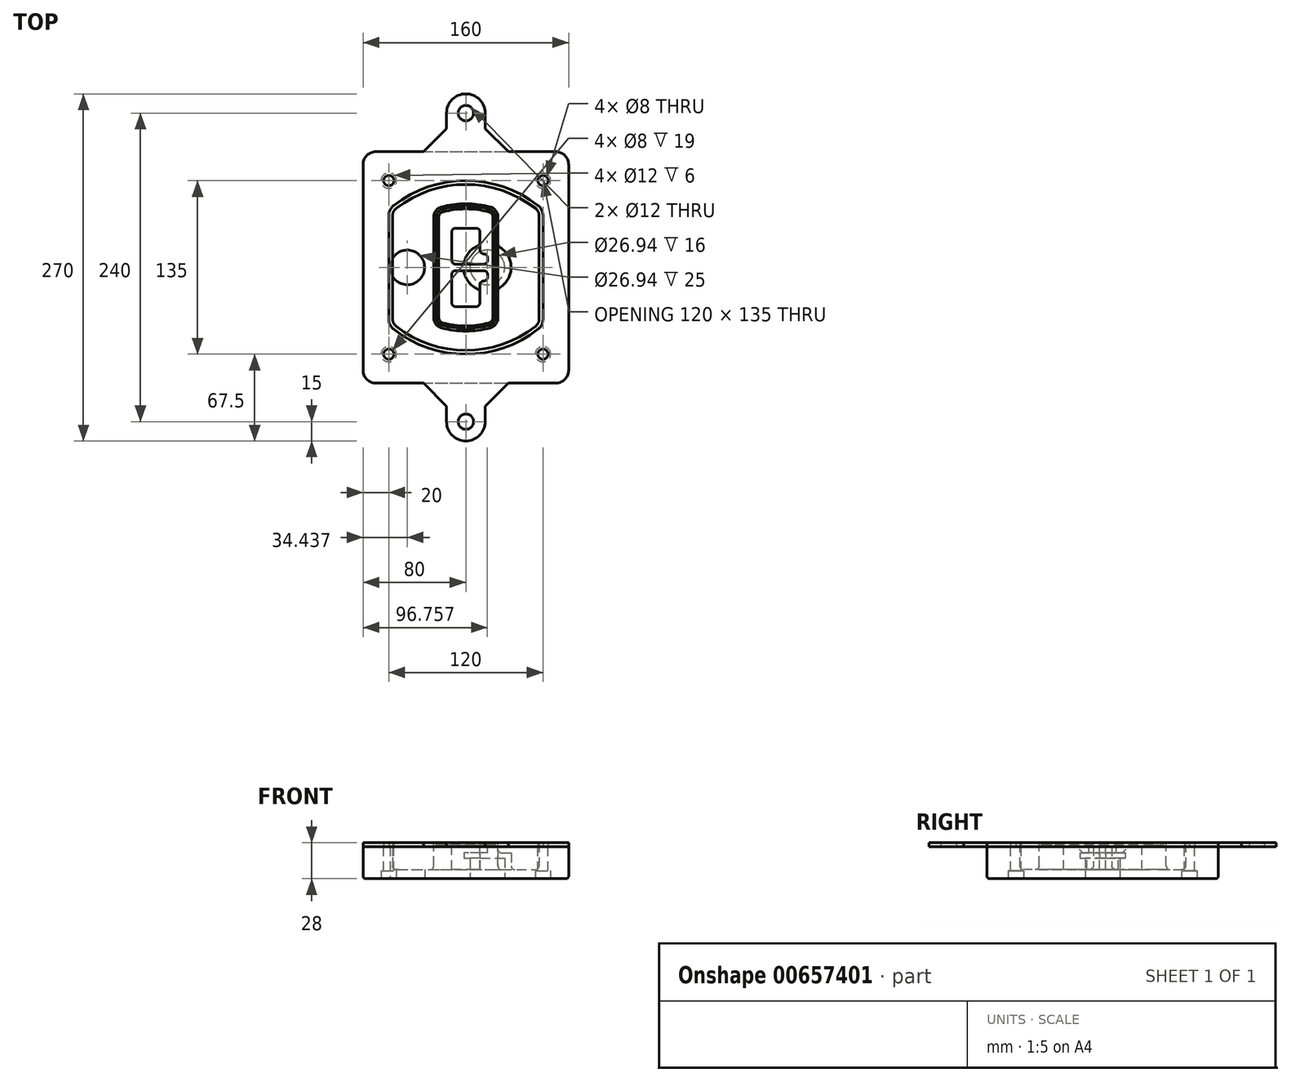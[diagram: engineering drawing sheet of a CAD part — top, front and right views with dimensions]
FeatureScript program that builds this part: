
annotation { "Feature Type Name" : "Feature", "Feature Type Description" : "" }
export const myFeature = defineFeature(function(context is Context, id is Id, definition is map)
    precondition{}
    {
        {
            var Q0;
            Q0=qCreatedBy(makeId("Top.planeOp"),FACE);
            var sketch = newSketch(context, id + "F0", { "sketchPlane" : qUnion([Q0])});
            skPoint(sketch, "E0.rect.middle", {"position": v(0, 0) * mm});
            skLineSegment(sketch, "E1.bottom", {"start": v(-70, -90) * mm, "end": v(70, -90) * mm});
            skLineSegment(sketch, "E1.top", {"start": v(-70, 90) * mm, "end": v(70, 90) * mm});
            skLineSegment(sketch, "E1.left", {"start": v(-80, -80) * mm, "end": v(-80, 80) * mm});
            skLineSegment(sketch, "E1.right", {"start": v(80, -80) * mm, "end": v(80, 80) * mm});
            skLineSegment(sketch, "E2", {"start": v(-80, 90) * mm, "end": v(80, -90) * mm, "construction": true});
            skLineSegment(sketch, "E3", {"start": v(80, 90) * mm, "end": v(-80, -90) * mm, "construction": true});
            skCircle(sketch, "E4", {"center": v(-60, 67.5) * mm, "radius": 4 * mm});
            skCircle(sketch, "E5", {"center": v(60, 67.5) * mm, "radius": 4 * mm});
            skCircle(sketch, "E6", {"center": v(60, -67.5) * mm, "radius": 4 * mm});
            skCircle(sketch, "E7", {"center": v(-60, -67.5) * mm, "radius": 4 * mm});
            skLineSegment(sketch, "E8", {"start": v(-60, 67.5) * mm, "end": v(60, 67.5) * mm, "construction": true});
            skLineSegment(sketch, "E9", {"start": v(60, 67.5) * mm, "end": v(60, -67.5) * mm, "construction": true});
            skLineSegment(sketch, "E10", {"start": v(60, -67.5) * mm, "end": v(-60, -67.5) * mm, "construction": true});
            skLineSegment(sketch, "E11", {"start": v(-60, -67.5) * mm, "end": v(-60, 67.5) * mm, "construction": true});
            skLineSegment(sketch, "E12", {"start": v(-60, 40.3) * mm, "end": v(-60, -40.3) * mm});
            skLineSegment(sketch, "E13", {"start": v(60, 40.3) * mm, "end": v(60, -40.3) * mm});
            skArc(sketch, "E14", {"start": v(56.15, 48.18) * mm, "mid": v(0, 67.5) * mm, "end": v(-56.15, 48.18) * mm});
            skArc(sketch, "E15", {"start": v(-56.15, -48.18) * mm, "mid": v(0, -67.5) * mm, "end": v(56.15, -48.18) * mm});
            skLineSegment(sketch, "E16", {"start": v(-60, 0) * mm, "end": v(60, 0) * mm, "construction": true});
            skPoint(sketch, "E17.visualSharp", {"position": v(-60, -45) * mm});
            skArc(sketch, "E17.filletArc", {"start": v(-60, -40.3) * mm, "mid": v(-58.99, -44.68) * mm, "end": v(-56.15, -48.18) * mm});
            skPoint(sketch, "E18.visualSharp", {"position": v(-60, 45) * mm});
            skArc(sketch, "E18.filletArc", {"start": v(-56.15, 48.18) * mm, "mid": v(-58.99, 44.68) * mm, "end": v(-60, 40.3) * mm});
            skPoint(sketch, "E19.visualSharp", {"position": v(60, 45) * mm});
            skArc(sketch, "E19.filletArc", {"start": v(60, 40.3) * mm, "mid": v(58.99, 44.68) * mm, "end": v(56.15, 48.18) * mm});
            skPoint(sketch, "E20.visualSharp", {"position": v(60, -45) * mm});
            skArc(sketch, "E20.filletArc", {"start": v(56.15, -48.18) * mm, "mid": v(58.99, -44.68) * mm, "end": v(60, -40.3) * mm});
            skPoint(sketch, "E21.visualSharp", {"position": v(-80, 90) * mm});
            skArc(sketch, "E21.filletArc", {"start": v(-70, 90) * mm, "mid": v(-77.07, 87.07) * mm, "end": v(-80, 80) * mm});
            skPoint(sketch, "E22.visualSharp", {"position": v(80, 90) * mm});
            skArc(sketch, "E22.filletArc", {"start": v(80, 80) * mm, "mid": v(77.07, 87.07) * mm, "end": v(70, 90) * mm});
            skPoint(sketch, "E23.visualSharp", {"position": v(80, -90) * mm});
            skArc(sketch, "E23.filletArc", {"start": v(70, -90) * mm, "mid": v(77.07, -87.07) * mm, "end": v(80, -80) * mm});
            skPoint(sketch, "E24.visualSharp", {"position": v(-80, -90) * mm});
            skArc(sketch, "E24.filletArc", {"start": v(-80, -80) * mm, "mid": v(-77.07, -87.07) * mm, "end": v(-70, -90) * mm});
            skArc(sketch, "E25.0", {"start": v(57, 40.3) * mm, "mid": v(56.3, 43.36) * mm, "end": v(54.3, 45.81) * mm});
            skLineSegment(sketch, "E25.1", {"start": v(57, 40.3) * mm, "end": v(57, -40.3) * mm});
            skArc(sketch, "E25.2", {"start": v(54.3, -45.81) * mm, "mid": v(56.3, -43.36) * mm, "end": v(57, -40.3) * mm});
            skArc(sketch, "E25.3", {"start": v(-54.3, -45.81) * mm, "mid": v(0, -64.5) * mm, "end": v(54.3, -45.81) * mm});
            skArc(sketch, "E25.4", {"start": v(-57, -40.3) * mm, "mid": v(-56.3, -43.36) * mm, "end": v(-54.3, -45.81) * mm});
            skArc(sketch, "E25.5", {"start": v(54.3, 45.81) * mm, "mid": v(0, 64.5) * mm, "end": v(-54.3, 45.81) * mm});
            skLineSegment(sketch, "E25.6", {"start": v(-57, 40.3) * mm, "end": v(-57, -40.3) * mm});
            skArc(sketch, "E25.7", {"start": v(-54.3, 45.81) * mm, "mid": v(-56.3, 43.36) * mm, "end": v(-57, 40.3) * mm});
            skArc(sketch, "E26.0", {"start": v(-58.62, 51.33) * mm, "mid": v(-62.58, 46.43) * mm, "end": v(-64, 40.3) * mm});
            skArc(sketch, "E26.1", {"start": v(58.62, 51.33) * mm, "mid": v(0, 71.5) * mm, "end": v(-58.62, 51.33) * mm});
            skArc(sketch, "E26.2", {"start": v(64, 40.3) * mm, "mid": v(62.58, 46.43) * mm, "end": v(58.62, 51.33) * mm});
            skLineSegment(sketch, "E26.3", {"start": v(64, 40.3) * mm, "end": v(64, -40.3) * mm});
            skArc(sketch, "E26.4", {"start": v(58.62, -51.33) * mm, "mid": v(62.58, -46.43) * mm, "end": v(64, -40.3) * mm});
            skLineSegment(sketch, "E26.5", {"start": v(-64, 40.3) * mm, "end": v(-64, -40.3) * mm});
            skArc(sketch, "E26.6", {"start": v(-58.62, -51.33) * mm, "mid": v(0, -71.5) * mm, "end": v(58.62, -51.33) * mm});
            skArc(sketch, "E26.7", {"start": v(-64, -40.3) * mm, "mid": v(-62.58, -46.43) * mm, "end": v(-58.62, -51.33) * mm});
            skSolve(sketch);
        }
        {
            var Q0;
            Q0=makeQuery(id+"F0.imprint","IMPRINT",FACE,{"disambiguationData":[TD([[makeQuery(id+"F0.imprint","IMPRINT",EDGE,{"derivedFrom":sQuery(id+"F0.wireOp",EDGE,"E1.bottom")}),1.0]])]});
            var Q1;
            Q1=makeQuery(id+"F0.imprint","IMPRINT",FACE,{"disambiguationData":[TD([[makeQuery(id+"F0.imprint","IMPRINT",EDGE,{"derivedFrom":sQuery(id+"F0.wireOp",EDGE,"E12")}),1.0]])]});
            var Q2;
            Q2=makeQuery(id+"F0.imprint","IMPRINT",FACE,{"disambiguationData":[TD([[makeQuery(id+"F0.imprint","IMPRINT",EDGE,{"derivedFrom":sQuery(id+"F0.wireOp",EDGE,"E25.0")}),1.0]])]});
            var Q3;
            Q3=makeQuery(id+"F0.imprint","IMPRINT",FACE,{"disambiguationData":[TD([[makeQuery(id+"F0.imprint","IMPRINT",EDGE,{"derivedFrom":sQuery(id+"F0.wireOp",EDGE,"E12")}),-1.0]])]});
            extrude(context, id + "F1", {"entities" : qUnion([Q0, Q1, Q2, Q3]), "oppositeDirection" : true, "depth" : 25 * mm});
        }
        {
            var Q0;
            Q0=makeQuery(id+"F0.imprint","IMPRINT",FACE,{"disambiguationData":[TD([[makeQuery(id+"F0.imprint","IMPRINT",EDGE,{"derivedFrom":sQuery(id+"F0.wireOp",EDGE,"E12")}),1.0]])]});
            extrude(context, id + "F2", {"entities" : qUnion([Q0]), "operationType" : NewBodyOperationType.ADD, "depth" : 3 * mm});
        }
        {
            var Q0;
            Q0=makeQuery(id+"F0.imprint","IMPRINT",FACE,{"disambiguationData":[TD([[makeQuery(id+"F0.imprint","IMPRINT",EDGE,{"derivedFrom":sQuery(id+"F0.wireOp",EDGE,"E25.0")}),1.0]])]});
            extrude(context, id + "F3", {"entities" : qUnion([Q0]), "operationType" : NewBodyOperationType.REMOVE, "oppositeDirection" : true, "depth" : 18 * mm});
        }
        {
            var Q0;
            Q0=makeQuery(id+"F2.opExtrude","CAP_FACE",FACE,{"disambiguationData":[OSD([sQuery(id+"F0.wireOp",EDGE,"E12"),sQuery(id+"F0.wireOp",EDGE,"E13"),sQuery(id+"F0.wireOp",EDGE,"E14"),sQuery(id+"F0.wireOp",EDGE,"E15"),sQuery(id+"F0.wireOp",EDGE,"E17.filletArc"),sQuery(id+"F0.wireOp",EDGE,"E18.filletArc"),sQuery(id+"F0.wireOp",EDGE,"E19.filletArc"),sQuery(id+"F0.wireOp",EDGE,"E20.filletArc"),sQuery(id+"F0.wireOp",EDGE,"E25.0"),sQuery(id+"F0.wireOp",EDGE,"E25.1"),sQuery(id+"F0.wireOp",EDGE,"E25.2"),sQuery(id+"F0.wireOp",EDGE,"E25.3"),sQuery(id+"F0.wireOp",EDGE,"E25.4"),sQuery(id+"F0.wireOp",EDGE,"E25.5"),sQuery(id+"F0.wireOp",EDGE,"E25.6"),sQuery(id+"F0.wireOp",EDGE,"E25.7")])],"isStart":false});
            var sketch = newSketch(context, id + "F4", { "sketchPlane" : qUnion([Q0])});
            skArc(sketch, "E27.0", {"start": v(-19.08, -46.97) * mm, "mid": v(0, -49.5) * mm, "end": v(19.08, -46.97) * mm});
            skArc(sketch, "E28.0", {"start": v(19.08, 46.97) * mm, "mid": v(0, 49.5) * mm, "end": v(-19.08, 46.97) * mm});
            skLineSegment(sketch, "E29", {"start": v(-25, 39.25) * mm, "end": v(-25, -39.25) * mm});
            skLineSegment(sketch, "E30", {"start": v(25, 39.25) * mm, "end": v(25, -39.25) * mm});
            skLineSegment(sketch, "E31", {"start": v(-25, 45.1) * mm, "end": v(25, 45.1) * mm, "construction": true});
            skLineSegment(sketch, "E32", {"start": v(-25, -45.1) * mm, "end": v(25, -45.1) * mm, "construction": true});
            skPoint(sketch, "E33.visualSharp", {"position": v(-25, 45.1) * mm});
            skArc(sketch, "E33.filletArc", {"start": v(-19.08, 46.97) * mm, "mid": v(-23.35, 44.11) * mm, "end": v(-25, 39.25) * mm});
            skPoint(sketch, "E34.visualSharp", {"position": v(25, 45.1) * mm});
            skArc(sketch, "E34.filletArc", {"start": v(25, 39.25) * mm, "mid": v(23.35, 44.11) * mm, "end": v(19.08, 46.97) * mm});
            skPoint(sketch, "E35.visualSharp", {"position": v(25, -45.1) * mm});
            skArc(sketch, "E35.filletArc", {"start": v(19.08, -46.97) * mm, "mid": v(23.35, -44.11) * mm, "end": v(25, -39.25) * mm});
            skPoint(sketch, "E36.visualSharp", {"position": v(-25, -45.1) * mm});
            skArc(sketch, "E36.filletArc", {"start": v(-25, -39.25) * mm, "mid": v(-23.35, -44.11) * mm, "end": v(-19.08, -46.97) * mm});
            skArc(sketch, "E37.0", {"start": v(54.3, 45.81) * mm, "mid": v(0, 64.5) * mm, "end": v(-54.3, 45.81) * mm});
            skArc(sketch, "E37.1", {"start": v(-54.3, 45.81) * mm, "mid": v(-56.3, 43.36) * mm, "end": v(-57, 40.3) * mm});
            skLineSegment(sketch, "E37.2", {"start": v(-57, 40.3) * mm, "end": v(-57, -40.3) * mm});
            skArc(sketch, "E37.3", {"start": v(-57, -40.3) * mm, "mid": v(-56.3, -43.36) * mm, "end": v(-54.3, -45.81) * mm});
            skArc(sketch, "E37.4", {"start": v(-54.3, -45.81) * mm, "mid": v(0, -64.5) * mm, "end": v(54.3, -45.81) * mm});
            skArc(sketch, "E37.5", {"start": v(54.3, -45.81) * mm, "mid": v(56.3, -43.36) * mm, "end": v(57, -40.3) * mm});
            skLineSegment(sketch, "E37.6", {"start": v(57, 40.3) * mm, "end": v(57, -40.3) * mm});
            skArc(sketch, "E37.7", {"start": v(57, 40.3) * mm, "mid": v(56.3, 43.36) * mm, "end": v(54.3, 45.81) * mm});
            skLineSegment(sketch, "E38.0", {"start": v(23, 39.25) * mm, "end": v(23, -39.25) * mm});
            skArc(sketch, "E38.1", {"start": v(18.56, -45.04) * mm, "mid": v(21.76, -42.9) * mm, "end": v(23, -39.25) * mm});
            skArc(sketch, "E38.2", {"start": v(-18.56, -45.04) * mm, "mid": v(0, -47.5) * mm, "end": v(18.56, -45.04) * mm});
            skArc(sketch, "E38.3", {"start": v(-23, -39.25) * mm, "mid": v(-21.76, -42.9) * mm, "end": v(-18.56, -45.04) * mm});
            skLineSegment(sketch, "E38.4", {"start": v(-23, 39.25) * mm, "end": v(-23, -39.25) * mm});
            skArc(sketch, "E38.5", {"start": v(23, 39.25) * mm, "mid": v(21.76, 42.9) * mm, "end": v(18.56, 45.04) * mm});
            skArc(sketch, "E38.6", {"start": v(-18.56, 45.04) * mm, "mid": v(-21.76, 42.9) * mm, "end": v(-23, 39.25) * mm});
            skArc(sketch, "E38.7", {"start": v(18.56, 45.04) * mm, "mid": v(0, 47.5) * mm, "end": v(-18.56, 45.04) * mm});
            skArc(sketch, "E39.0", {"start": v(21, 39.25) * mm, "mid": v(20.18, 41.68) * mm, "end": v(18.04, 43.1) * mm});
            skLineSegment(sketch, "E39.1", {"start": v(21, 39.25) * mm, "end": v(21, -39.25) * mm});
            skArc(sketch, "E39.2", {"start": v(18.04, -43.1) * mm, "mid": v(20.18, -41.68) * mm, "end": v(21, -39.25) * mm});
            skArc(sketch, "E39.3", {"start": v(-18.04, -43.1) * mm, "mid": v(0, -45.5) * mm, "end": v(18.04, -43.1) * mm});
            skArc(sketch, "E39.4", {"start": v(-21, -39.25) * mm, "mid": v(-20.18, -41.68) * mm, "end": v(-18.04, -43.1) * mm});
            skArc(sketch, "E39.5", {"start": v(18.04, 43.1) * mm, "mid": v(0, 45.5) * mm, "end": v(-18.04, 43.1) * mm});
            skLineSegment(sketch, "E39.6", {"start": v(-21, 39.25) * mm, "end": v(-21, -39.25) * mm});
            skArc(sketch, "E39.7", {"start": v(-18.04, 43.1) * mm, "mid": v(-20.18, 41.68) * mm, "end": v(-21, 39.25) * mm});
            skLineSegment(sketch, "E40", {"start": v(-25, 0) * mm, "end": v(25, 0) * mm, "construction": true});
            skLineSegment(sketch, "E41", {"start": v(-11, 5.5) * mm, "end": v(-11, 27.5) * mm});
            skLineSegment(sketch, "E42", {"start": v(-8, 30.5) * mm, "end": v(8, 30.5) * mm});
            skLineSegment(sketch, "E43", {"start": v(11, 27.5) * mm, "end": v(11, 13.5) * mm});
            skLineSegment(sketch, "E44", {"start": v(14, 10.5) * mm, "end": v(14, 10.5) * mm});
            skLineSegment(sketch, "E45", {"start": v(17, 7.5) * mm, "end": v(17, 5.5) * mm});
            skLineSegment(sketch, "E46", {"start": v(14, 2.5) * mm, "end": v(-8, 2.5) * mm});
            skPoint(sketch, "E47.visualSharp", {"position": v(-11, 30.5) * mm});
            skArc(sketch, "E47.filletArc", {"start": v(-8, 30.5) * mm, "mid": v(-10.12, 29.62) * mm, "end": v(-11, 27.5) * mm});
            skPoint(sketch, "E48.visualSharp", {"position": v(11, 30.5) * mm});
            skArc(sketch, "E48.filletArc", {"start": v(11, 27.5) * mm, "mid": v(10.12, 29.62) * mm, "end": v(8, 30.5) * mm});
            skPoint(sketch, "E49.visualSharp", {"position": v(11, 10.5) * mm});
            skArc(sketch, "E49.filletArc", {"start": v(11, 13.5) * mm, "mid": v(11.88, 11.38) * mm, "end": v(14, 10.5) * mm});
            skPoint(sketch, "E50.visualSharp", {"position": v(17, 10.5) * mm});
            skArc(sketch, "E50.filletArc", {"start": v(17, 7.5) * mm, "mid": v(16.12, 9.62) * mm, "end": v(14, 10.5) * mm});
            skPoint(sketch, "E51.visualSharp", {"position": v(17, 2.5) * mm});
            skArc(sketch, "E51.filletArc", {"start": v(14, 2.5) * mm, "mid": v(16.12, 3.38) * mm, "end": v(17, 5.5) * mm});
            skPoint(sketch, "E52.visualSharp", {"position": v(-11, 2.5) * mm});
            skArc(sketch, "E52.filletArc", {"start": v(-11, 5.5) * mm, "mid": v(-10.12, 3.38) * mm, "end": v(-8, 2.5) * mm});
            skLineSegment(sketch, "E53.0.MirrorCS", {"start": v(14, -2.5) * mm, "end": v(-8, -2.5) * mm});
            skArc(sketch, "E54.0.MirrorCS", {"start": v(-11, -5.5) * mm, "mid": v(-10.12, -3.38) * mm, "end": v(-8, -2.5) * mm});
            skLineSegment(sketch, "E55.0.MirrorCS", {"start": v(-11, -5.5) * mm, "end": v(-11, -27.5) * mm});
            skArc(sketch, "E56.0.MirrorCS", {"start": v(-8, -30.5) * mm, "mid": v(-10.12, -29.62) * mm, "end": v(-11, -27.5) * mm});
            skLineSegment(sketch, "E57.0.MirrorCS", {"start": v(-8, -30.5) * mm, "end": v(8, -30.5) * mm});
            skArc(sketch, "E58.0.MirrorCS", {"start": v(11, -27.5) * mm, "mid": v(10.12, -29.62) * mm, "end": v(8, -30.5) * mm});
            skLineSegment(sketch, "E59.0.MirrorCS", {"start": v(11, -27.5) * mm, "end": v(11, -13.5) * mm});
            skArc(sketch, "E60.0.MirrorCS", {"start": v(11, -13.5) * mm, "mid": v(11.88, -11.38) * mm, "end": v(14, -10.5) * mm});
            skArc(sketch, "E61.0.MirrorCS", {"start": v(17, -7.5) * mm, "mid": v(16.12, -9.62) * mm, "end": v(14, -10.5) * mm});
            skLineSegment(sketch, "E62.0.MirrorCS", {"start": v(17, -7.5) * mm, "end": v(17, -5.5) * mm});
            skArc(sketch, "E63.0.MirrorCS", {"start": v(14, -2.5) * mm, "mid": v(16.12, -3.38) * mm, "end": v(17, -5.5) * mm});
            skSolve(sketch);
        }
        {
            var Q0;
            Q0=makeQuery(id+"F4.imprint","IMPRINT",FACE,{"disambiguationData":[TD([[makeQuery(id+"F4.imprint","IMPRINT",EDGE,{"derivedFrom":sQuery(id+"F4.wireOp",EDGE,"E27.0")}),1.0]])]});
            var Q1;
            Q1=makeQuery(id+"F4.imprint","IMPRINT",FACE,{"disambiguationData":[TD([[makeQuery(id+"F4.imprint","IMPRINT",EDGE,{"derivedFrom":sQuery(id+"F4.wireOp",EDGE,"E38.0")}),-1.0]])]});
            var Q2;
            Q2=makeQuery(id+"F4.imprint","IMPRINT",FACE,{"disambiguationData":[TD([[makeQuery(id+"F4.imprint","IMPRINT",EDGE,{"derivedFrom":sQuery(id+"F4.wireOp",EDGE,"E39.0")}),1.0]])]});
            extrude(context, id + "F5", {"entities" : qUnion([Q0, Q1, Q2]), "operationType" : NewBodyOperationType.ADD, "endBound" : BoundingType.UP_TO_NEXT, "oppositeDirection" : true, "depth" : 25 * mm});
        }
        {
            var Q0;
            Q0=makeQuery(id+"F4.imprint","IMPRINT",FACE,{"disambiguationData":[TD([[makeQuery(id+"F4.imprint","IMPRINT",EDGE,{"derivedFrom":sQuery(id+"F4.wireOp",EDGE,"E38.0")}),-1.0]])]});
            extrude(context, id + "F6", {"entities" : qUnion([Q0]), "operationType" : NewBodyOperationType.REMOVE, "oppositeDirection" : true, "depth" : 2 * mm});
        }
        {
            var Q0;
            Q0=makeQuery(id+"F1.opExtrude","CAP_FACE",FACE,{"disambiguationData":[OSD([sQuery(id+"F0.wireOp",EDGE,"E1.bottom"),sQuery(id+"F0.wireOp",EDGE,"E1.top"),sQuery(id+"F0.wireOp",EDGE,"E1.left"),sQuery(id+"F0.wireOp",EDGE,"E1.right"),sQuery(id+"F0.wireOp",EDGE,"E4"),sQuery(id+"F0.wireOp",EDGE,"E5"),sQuery(id+"F0.wireOp",EDGE,"E6"),sQuery(id+"F0.wireOp",EDGE,"E7"),sQuery(id+"F0.wireOp",EDGE,"E21.filletArc"),sQuery(id+"F0.wireOp",EDGE,"E22.filletArc"),sQuery(id+"F0.wireOp",EDGE,"E23.filletArc"),sQuery(id+"F0.wireOp",EDGE,"E24.filletArc")])],"isStart":false});
            var sketch = newSketch(context, id + "F7", { "sketchPlane" : qUnion([Q0])});
            skCircle(sketch, "E64", {"center": v(16.76, 0) * mm, "radius": 13.47 * mm});
            skCircle(sketch, "E65", {"center": v(-45.56, 0) * mm, "radius": 13.47 * mm});
            skLineSegment(sketch, "E66", {"start": v(80, 0) * mm, "end": v(-80, 0) * mm});
            skCircle(sketch, "E67", {"center": v(16.76, 0) * mm, "radius": 18.47 * mm});
            skCircle(sketch, "E68", {"center": v(60, -67.5) * mm, "radius": 6 * mm});
            skCircle(sketch, "E69", {"center": v(-60, -67.5) * mm, "radius": 6 * mm});
            skCircle(sketch, "E70", {"center": v(-60, 67.5) * mm, "radius": 6 * mm});
            skCircle(sketch, "E71", {"center": v(60, 67.5) * mm, "radius": 6 * mm});
            skSolve(sketch);
        }
        {
            var Q0;
            {var subQ1=sQuery(id+"F7.wireOp",EDGE,"E66");var subQ4=sQuery(id+"F7.wireOp",EDGE,"E64");var subQ6=makeQuery(id+"F7.imprint","INTERSECT",VERTEX,{"disambiguationData":[OD(0.0)],"derivedFrom":[subQ4,subQ1]});Q0=makeQuery(id+"F7.imprint","IMPRINT",FACE,{"disambiguationData":[TD([[makeQuery(id+"F7.imprint","IMPRINT",EDGE,{"disambiguationData":[TD([[subQ6,-1.0]])],"derivedFrom":subQ4}),-1.0]])]});}
            var Q1;
            {var subQ0=sQuery(id+"F7.wireOp",EDGE,"E66");var subQ1=sQuery(id+"F7.wireOp",EDGE,"E64");var subQ3=makeQuery(id+"F7.imprint","INTERSECT",VERTEX,{"disambiguationData":[OD(0.0)],"derivedFrom":[subQ1,subQ0]});Q1=makeQuery(id+"F7.imprint","IMPRINT",FACE,{"disambiguationData":[TD([[makeQuery(id+"F7.imprint","IMPRINT",EDGE,{"disambiguationData":[TD([[subQ3,-1.0]])],"derivedFrom":subQ1}),1.0]])]});}
            var Q2;
            {var subQ0=sQuery(id+"F7.wireOp",EDGE,"E66");var subQ1=sQuery(id+"F7.wireOp",EDGE,"E64");var subQ3=makeQuery(id+"F7.imprint","INTERSECT",VERTEX,{"disambiguationData":[OD(0.0)],"derivedFrom":[subQ1,subQ0]});Q2=makeQuery(id+"F7.imprint","IMPRINT",FACE,{"disambiguationData":[TD([[makeQuery(id+"F7.imprint","IMPRINT",EDGE,{"disambiguationData":[TD([[subQ3,1.0]])],"derivedFrom":subQ1}),1.0]])]});}
            var Q3;
            {var subQ1=sQuery(id+"F7.wireOp",EDGE,"E66");var subQ4=sQuery(id+"F7.wireOp",EDGE,"E64");var subQ6=makeQuery(id+"F7.imprint","INTERSECT",VERTEX,{"disambiguationData":[OD(0.0)],"derivedFrom":[subQ4,subQ1]});Q3=makeQuery(id+"F7.imprint","IMPRINT",FACE,{"disambiguationData":[TD([[makeQuery(id+"F7.imprint","IMPRINT",EDGE,{"disambiguationData":[TD([[subQ6,1.0]])],"derivedFrom":subQ4}),-1.0]])]});}
            extrude(context, id + "F8", {"entities" : qUnion([Q0, Q1, Q2, Q3]), "operationType" : NewBodyOperationType.ADD, "oppositeDirection" : true, "depth" : 20 * mm});
        }
        {
            var Q0;
            {var subQ0=sQuery(id+"F7.wireOp",EDGE,"E66");var subQ1=sQuery(id+"F7.wireOp",EDGE,"E64");var subQ3=makeQuery(id+"F7.imprint","INTERSECT",VERTEX,{"disambiguationData":[OD(0.0)],"derivedFrom":[subQ1,subQ0]});Q0=makeQuery(id+"F7.imprint","IMPRINT",FACE,{"disambiguationData":[TD([[makeQuery(id+"F7.imprint","IMPRINT",EDGE,{"disambiguationData":[TD([[subQ3,-1.0]])],"derivedFrom":subQ1}),1.0]])]});}
            var Q1;
            {var subQ0=sQuery(id+"F7.wireOp",EDGE,"E66");var subQ1=sQuery(id+"F7.wireOp",EDGE,"E64");var subQ3=makeQuery(id+"F7.imprint","INTERSECT",VERTEX,{"disambiguationData":[OD(0.0)],"derivedFrom":[subQ1,subQ0]});Q1=makeQuery(id+"F7.imprint","IMPRINT",FACE,{"disambiguationData":[TD([[makeQuery(id+"F7.imprint","IMPRINT",EDGE,{"disambiguationData":[TD([[subQ3,1.0]])],"derivedFrom":subQ1}),1.0]])]});}
            extrude(context, id + "F9", {"entities" : qUnion([Q0, Q1]), "operationType" : NewBodyOperationType.REMOVE, "oppositeDirection" : true, "depth" : 16 * mm});
        }
        {
            var Q0;
            {var subQ0=sQuery(id+"F7.wireOp",EDGE,"E66");var subQ1=sQuery(id+"F7.wireOp",EDGE,"E65");var subQ3=makeQuery(id+"F7.imprint","INTERSECT",VERTEX,{"disambiguationData":[OD(0.0)],"derivedFrom":[subQ1,subQ0]});Q0=makeQuery(id+"F7.imprint","IMPRINT",FACE,{"disambiguationData":[TD([[makeQuery(id+"F7.imprint","IMPRINT",EDGE,{"disambiguationData":[TD([[subQ3,-1.0]])],"derivedFrom":subQ1}),1.0]])]});}
            var Q1;
            {var subQ0=sQuery(id+"F7.wireOp",EDGE,"E66");var subQ1=sQuery(id+"F7.wireOp",EDGE,"E65");var subQ3=makeQuery(id+"F7.imprint","INTERSECT",VERTEX,{"disambiguationData":[OD(0.0)],"derivedFrom":[subQ1,subQ0]});Q1=makeQuery(id+"F7.imprint","IMPRINT",FACE,{"disambiguationData":[TD([[makeQuery(id+"F7.imprint","IMPRINT",EDGE,{"disambiguationData":[TD([[subQ3,1.0]])],"derivedFrom":subQ1}),1.0]])]});}
            extrude(context, id + "F10", {"entities" : qUnion([Q0, Q1]), "operationType" : NewBodyOperationType.REMOVE, "oppositeDirection" : true, "depth" : 25 * mm});
        }
        {
            var Q0;
            Q0=makeQuery(id+"F7.imprint","IMPRINT",FACE,{"disambiguationData":[TD([[makeQuery(id+"F7.imprint","IMPRINT",EDGE,{"derivedFrom":sQuery(id+"F7.wireOp",EDGE,"E68")}),1.0]])]});
            var Q1;
            Q1=makeQuery(id+"F7.imprint","IMPRINT",FACE,{"disambiguationData":[TD([[makeQuery(id+"F7.imprint","IMPRINT",EDGE,{"derivedFrom":makeQuery(id+"F1.opExtrude","CAP_EDGE",EDGE,{"disambiguationData":[OSD([sQuery(id+"F0.wireOp",EDGE,"E5")])],"isStart":false})}),-1.0]])]});
            var Q2;
            Q2=makeQuery(id+"F7.imprint","IMPRINT",FACE,{"disambiguationData":[TD([[makeQuery(id+"F7.imprint","IMPRINT",EDGE,{"derivedFrom":sQuery(id+"F7.wireOp",EDGE,"E69")}),1.0]])]});
            var Q3;
            Q3=makeQuery(id+"F7.imprint","IMPRINT",FACE,{"disambiguationData":[TD([[makeQuery(id+"F7.imprint","IMPRINT",EDGE,{"derivedFrom":makeQuery(id+"F1.opExtrude","CAP_EDGE",EDGE,{"disambiguationData":[OSD([sQuery(id+"F0.wireOp",EDGE,"E4")])],"isStart":false})}),-1.0]])]});
            var Q4;
            Q4=makeQuery(id+"F7.imprint","IMPRINT",FACE,{"disambiguationData":[TD([[makeQuery(id+"F7.imprint","IMPRINT",EDGE,{"derivedFrom":sQuery(id+"F7.wireOp",EDGE,"E70")}),1.0]])]});
            var Q5;
            Q5=makeQuery(id+"F7.imprint","IMPRINT",FACE,{"disambiguationData":[TD([[makeQuery(id+"F7.imprint","IMPRINT",EDGE,{"derivedFrom":makeQuery(id+"F1.opExtrude","CAP_EDGE",EDGE,{"disambiguationData":[OSD([sQuery(id+"F0.wireOp",EDGE,"E7")])],"isStart":false})}),-1.0]])]});
            var Q6;
            Q6=makeQuery(id+"F7.imprint","IMPRINT",FACE,{"disambiguationData":[TD([[makeQuery(id+"F7.imprint","IMPRINT",EDGE,{"derivedFrom":sQuery(id+"F7.wireOp",EDGE,"E71")}),1.0]])]});
            var Q7;
            Q7=makeQuery(id+"F7.imprint","IMPRINT",FACE,{"disambiguationData":[TD([[makeQuery(id+"F7.imprint","IMPRINT",EDGE,{"derivedFrom":makeQuery(id+"F1.opExtrude","CAP_EDGE",EDGE,{"disambiguationData":[OSD([sQuery(id+"F0.wireOp",EDGE,"E6")])],"isStart":false})}),-1.0]])]});
            extrude(context, id + "F11", {"entities" : qUnion([Q0, Q1, Q2, Q3, Q4, Q5, Q6, Q7]), "operationType" : NewBodyOperationType.REMOVE, "oppositeDirection" : true, "depth" : 6 * mm});
        }
        {
            var Q0;
            Q0=makeQuery(id+"F9.boolean.opBoolean","COPY",FACE,{"derivedFrom":makeQuery(id+"F9.opExtrude","CAP_FACE",FACE,{"disambiguationData":[OSD([sQuery(id+"F7.wireOp",EDGE,"E64")])],"isStart":false})});
            var sketch = newSketch(context, id + "F12", { "sketchPlane" : qUnion([Q0])});
            skArc(sketch, "E72.0", {"start": v(11, 17.55) * mm, "mid": v(2.57, 11.82) * mm, "end": v(-1.54, 2.5) * mm});
            skArc(sketch, "E72.1", {"start": v(-1.54, -2.5) * mm, "mid": v(2.57, -11.82) * mm, "end": v(11, -17.55) * mm});
            skLineSegment(sketch, "E73", {"start": v(-1.54, -2.5) * mm, "end": v(14, -2.5) * mm});
            skLineSegment(sketch, "E74.0", {"start": v(14, 2.5) * mm, "end": v(-1.54, 2.5) * mm});
            skArc(sketch, "E74.1", {"start": v(14, 2.5) * mm, "mid": v(16.12, 3.38) * mm, "end": v(17, 5.5) * mm});
            skLineSegment(sketch, "E74.2", {"start": v(17, 7.5) * mm, "end": v(17, 5.5) * mm});
            skArc(sketch, "E74.3", {"start": v(17, 7.5) * mm, "mid": v(16.12, 9.62) * mm, "end": v(14, 10.5) * mm});
            skArc(sketch, "E74.4", {"start": v(11, 13.5) * mm, "mid": v(11.88, 11.38) * mm, "end": v(14, 10.5) * mm});
            skLineSegment(sketch, "E74.5", {"start": v(11, 17.55) * mm, "end": v(11, 13.5) * mm});
            skLineSegment(sketch, "E74.7", {"start": v(14, -2.5) * mm, "end": v(-1.54, -2.5) * mm});
            skArc(sketch, "E74.8", {"start": v(14, -2.5) * mm, "mid": v(16.12, -3.38) * mm, "end": v(17, -5.5) * mm});
            skLineSegment(sketch, "E74.9", {"start": v(17, -7.5) * mm, "end": v(17, -5.5) * mm});
            skArc(sketch, "E74.10", {"start": v(17, -7.5) * mm, "mid": v(16.12, -9.62) * mm, "end": v(14, -10.5) * mm});
            skArc(sketch, "E74.11", {"start": v(11, -13.5) * mm, "mid": v(11.88, -11.38) * mm, "end": v(14, -10.5) * mm});
            skLineSegment(sketch, "E74.12", {"start": v(11, -17.55) * mm, "end": v(11, -13.5) * mm});
            skPoint(sketch, "E75.orphan", {"position": v(11, -27.5) * mm});
            skPoint(sketch, "E76.orphan", {"position": v(-8, -2.5) * mm});
            skPoint(sketch, "E77.orphan", {"position": v(-8, 2.5) * mm});
            skPoint(sketch, "E78.orphan", {"position": v(11, 27.5) * mm});
            skSolve(sketch);
        }
        {
            var Q0;
            {var subQ7=sQuery(id+"F12.wireOp",EDGE,"E72.0");var subQ14=sQuery(id+"F12.wireOp",EDGE,"E72.1");var subQ16=sQuery(id+"F12.wireOp",EDGE,"E74.1");var subQ18=sQuery(id+"F12.wireOp",EDGE,"E74.8");Q0=qUnion([makeQuery(id+"F12.imprint","IMPRINT",FACE,{"disambiguationData":[TD([[makeQuery(id+"F12.imprint","IMPRINT",EDGE,{"derivedFrom":subQ7}),1.0]])]}),makeQuery(id+"F12.imprint","IMPRINT",FACE,{"disambiguationData":[TD([[makeQuery(id+"F12.imprint","IMPRINT",EDGE,{"derivedFrom":subQ14}),1.0]])]}),makeQuery(id+"F12.imprint","IMPRINT",FACE,{"disambiguationData":[TD([[makeQuery(id+"F12.imprint","IMPRINT",EDGE,{"derivedFrom":subQ16}),1.0]])]}),makeQuery(id+"F12.imprint","IMPRINT",FACE,{"disambiguationData":[TD([[makeQuery(id+"F12.imprint","IMPRINT",EDGE,{"derivedFrom":subQ18}),-1.0]])]})]);}
            var Q1;
            Q1=makeQuery(id+"F5.boolean.opBoolean","SPLIT",FACE,{"disambiguationData":[TD([makeQuery(id+"F5.opExtrude","SWEPT_FACE",FACE,{"disambiguationData":[OSD([sQuery(id+"F4.wireOp",EDGE,"E41")])]})])],"derivedFrom":makeQuery(id+"F3.boolean.opBoolean","COPY",FACE,{"derivedFrom":makeQuery(id+"F3.opExtrude","CAP_FACE",FACE,{"disambiguationData":[OSD([sQuery(id+"F0.wireOp",EDGE,"E25.0"),sQuery(id+"F0.wireOp",EDGE,"E25.1"),sQuery(id+"F0.wireOp",EDGE,"E25.2"),sQuery(id+"F0.wireOp",EDGE,"E25.3"),sQuery(id+"F0.wireOp",EDGE,"E25.4"),sQuery(id+"F0.wireOp",EDGE,"E25.5"),sQuery(id+"F0.wireOp",EDGE,"E25.6"),sQuery(id+"F0.wireOp",EDGE,"E25.7")])],"isStart":false})})});
            extrude(context, id + "F13", {"entities" : qUnion([Q0]), "operationType" : NewBodyOperationType.REMOVE, "endBound" : BoundingType.UP_TO_SURFACE, "endBoundEntityFace" : qUnion([Q1]), "depth" : 25 * mm});
        }
        {
            var Q0;
            Q0=makeQuery(id+"F3.boolean.opBoolean","COPY",EDGE,{"derivedFrom":makeQuery(id+"F3.opExtrude","CAP_EDGE",EDGE,{"disambiguationData":[OSD([sQuery(id+"F0.wireOp",EDGE,"E25.6")])],"isStart":false})});
            var Q1;
            Q1=makeQuery(id+"F8.boolean.opBoolean","INTERSECT",EDGE,{"derivedFrom":[makeQuery(id+"F5.opExtrude","SWEPT_FACE",FACE,{"disambiguationData":[OSD([sQuery(id+"F4.wireOp",EDGE,"E30")])]}),makeQuery(id+"F8.opExtrude","CAP_FACE",FACE,{"disambiguationData":[OSD([sQuery(id+"F7.wireOp",EDGE,"E67")])],"isStart":false})]});
            var Q2;
            Q2=makeQuery(id+"F8.boolean.opBoolean","INTERSECT",EDGE,{"disambiguationData":[OD(1.0)],"derivedFrom":[makeQuery(id+"F5.opExtrude","SWEPT_FACE",FACE,{"disambiguationData":[OSD([sQuery(id+"F4.wireOp",EDGE,"E30")])]}),makeQuery(id+"F8.opExtrude","SWEPT_FACE",FACE,{"disambiguationData":[OSD([sQuery(id+"F7.wireOp",EDGE,"E67")])]})]});
            var Q3;
            {var subQ0=sQuery(id+"F4.wireOp",EDGE,"E30");Q3=makeQuery(id+"F8.boolean.opBoolean","SPLIT",EDGE,{"disambiguationData":[TD([makeQuery(id+"F5.opExtrude","SWEPT_FACE",FACE,{"disambiguationData":[OSD([sQuery(id+"F4.wireOp",EDGE,"E35.filletArc")])]})])],"derivedFrom":makeQuery(id+"F5.opExtrude","CAP_EDGE",EDGE,{"disambiguationData":[OSD([subQ0])],"isStart":false})});}
            var Q4;
            {var subQ0=sQuery(id+"F0.wireOp",EDGE,"E25.7");var subQ1=sQuery(id+"F0.wireOp",EDGE,"E25.1");var subQ2=sQuery(id+"F0.wireOp",EDGE,"E25.6");var subQ3=sQuery(id+"F0.wireOp",EDGE,"E25.5");var subQ4=sQuery(id+"F0.wireOp",EDGE,"E25.4");var subQ5=sQuery(id+"F0.wireOp",EDGE,"E25.0");var subQ6=sQuery(id+"F0.wireOp",EDGE,"E25.2");var subQ7=sQuery(id+"F0.wireOp",EDGE,"E25.3");Q4=makeQuery(id+"F8.boolean.opBoolean","INTERSECT",EDGE,{"derivedFrom":[makeQuery(id+"F5.boolean.opBoolean","SPLIT",FACE,{"disambiguationData":[TD([makeQuery(id+"F2.opExtrude","SWEPT_FACE",FACE,{"disambiguationData":[OSD([subQ5])]})])],"derivedFrom":makeQuery(id+"F3.boolean.opBoolean","COPY",FACE,{"derivedFrom":makeQuery(id+"F3.opExtrude","CAP_FACE",FACE,{"disambiguationData":[OSD([subQ5,subQ1,subQ6,subQ7,subQ4,subQ3,subQ2,subQ0])],"isStart":false})})}),makeQuery(id+"F8.opExtrude","SWEPT_FACE",FACE,{"disambiguationData":[OSD([sQuery(id+"F7.wireOp",EDGE,"E67")])]})]});}
            var Q5;
            Q5=makeQuery(id+"F8.boolean.opBoolean","INTERSECT",EDGE,{"disambiguationData":[OD(0.0)],"derivedFrom":[makeQuery(id+"F5.opExtrude","SWEPT_FACE",FACE,{"disambiguationData":[OSD([sQuery(id+"F4.wireOp",EDGE,"E30")])]}),makeQuery(id+"F8.opExtrude","SWEPT_FACE",FACE,{"disambiguationData":[OSD([sQuery(id+"F7.wireOp",EDGE,"E67")])]})]});
            fillet(context, id + "F14", {"entities" : qUnion([Q0, Q1, Q2, Q3, Q4, Q5]), "radius" : 3 * mm, "tangentPropagation" : true, "allowEdgeOverflow" : false});
        }
        {
            var Q0;
            Q0=makeQuery(id+"F1.opExtrude","CAP_EDGE",EDGE,{"disambiguationData":[OSD([sQuery(id+"F0.wireOp",EDGE,"E1.bottom")])],"isStart":false});
            fillet(context, id + "F15", {"entities" : qUnion([Q0]), "radius" : 2 * mm, "tangentPropagation" : true, "allowEdgeOverflow" : false});
        }
        {
            var Q0;
            {var subQ0=sQuery(id+"F0.wireOp",EDGE,"E21.filletArc");var subQ1=sQuery(id+"F0.wireOp",EDGE,"E7");var subQ2=sQuery(id+"F0.wireOp",EDGE,"E6");var subQ3=sQuery(id+"F0.wireOp",EDGE,"E5");var subQ4=sQuery(id+"F0.wireOp",EDGE,"E4");var subQ5=sQuery(id+"F0.wireOp",EDGE,"E22.filletArc");var subQ6=sQuery(id+"F0.wireOp",EDGE,"E1.bottom");var subQ7=sQuery(id+"F0.wireOp",EDGE,"E1.right");var subQ8=sQuery(id+"F0.wireOp",EDGE,"E1.top");var subQ9=sQuery(id+"F0.wireOp",EDGE,"E1.left");var subQ10=sQuery(id+"F0.wireOp",EDGE,"E23.filletArc");var subQ11=sQuery(id+"F0.wireOp",EDGE,"E24.filletArc");Q0=makeQuery(id+"F2.boolean.opBoolean","SPLIT",FACE,{"disambiguationData":[TD([makeQuery(id+"F1.opExtrude","SWEPT_FACE",FACE,{"disambiguationData":[OSD([subQ6])]})])],"derivedFrom":makeQuery(id+"F1.opExtrude","CAP_FACE",FACE,{"disambiguationData":[OSD([subQ6,subQ8,subQ9,subQ7,subQ4,subQ3,subQ2,subQ1,subQ0,subQ5,subQ10,subQ11])],"isStart":true})});}
            var sketch = newSketch(context, id + "F16", { "sketchPlane" : qUnion([Q0])});
            skLineSegment(sketch, "E79.0", {"start": v(-70, 90) * mm, "end": v(70, 90) * mm});
            skArc(sketch, "E79.1", {"start": v(80, 80) * mm, "mid": v(77.07, 87.07) * mm, "end": v(70, 90) * mm});
            skLineSegment(sketch, "E79.2", {"start": v(80, -80) * mm, "end": v(80, 80) * mm});
            skCircle(sketch, "E79.3", {"center": v(60, 67.5) * mm, "radius": 4 * mm});
            skCircle(sketch, "E79.4", {"center": v(-60, 67.5) * mm, "radius": 4 * mm});
            skLineSegment(sketch, "E79.5", {"start": v(-80, -80) * mm, "end": v(-80, 80) * mm});
            skArc(sketch, "E79.6", {"start": v(-70, 90) * mm, "mid": v(-77.07, 87.07) * mm, "end": v(-80, 80) * mm});
            skArc(sketch, "E79.7", {"start": v(70, -90) * mm, "mid": v(77.07, -87.07) * mm, "end": v(80, -80) * mm});
            skLineSegment(sketch, "E79.8", {"start": v(-70, -90) * mm, "end": v(70, -90) * mm});
            skArc(sketch, "E79.9", {"start": v(-80, -80) * mm, "mid": v(-77.07, -87.07) * mm, "end": v(-70, -90) * mm});
            skCircle(sketch, "E79.10", {"center": v(-60, -67.5) * mm, "radius": 4 * mm});
            skCircle(sketch, "E79.11", {"center": v(60, -67.5) * mm, "radius": 4 * mm});
            skArc(sketch, "E79.12", {"start": v(-56.15, -48.18) * mm, "mid": v(0, -67.5) * mm, "end": v(56.15, -48.18) * mm});
            skArc(sketch, "E79.13", {"start": v(56.15, -48.18) * mm, "mid": v(58.99, -44.68) * mm, "end": v(60, -40.3) * mm});
            skLineSegment(sketch, "E79.14", {"start": v(60, 40.3) * mm, "end": v(60, -40.3) * mm});
            skArc(sketch, "E79.15", {"start": v(60, 40.3) * mm, "mid": v(58.99, 44.68) * mm, "end": v(56.15, 48.18) * mm});
            skArc(sketch, "E79.16", {"start": v(56.15, 48.18) * mm, "mid": v(0, 67.5) * mm, "end": v(-56.15, 48.18) * mm});
            skArc(sketch, "E79.17", {"start": v(-56.15, 48.18) * mm, "mid": v(-58.99, 44.68) * mm, "end": v(-60, 40.3) * mm});
            skLineSegment(sketch, "E79.18", {"start": v(-60, 40.3) * mm, "end": v(-60, -40.3) * mm});
            skArc(sketch, "E79.19", {"start": v(-60, -40.3) * mm, "mid": v(-58.99, -44.68) * mm, "end": v(-56.15, -48.18) * mm});
            skLineSegment(sketch, "E80", {"start": v(0, 120) * mm, "end": v(0, 90) * mm, "construction": true});
            skPoint(sketch, "E80.startSnap0", {"position": v(0, 90) * mm});
            skCircle(sketch, "E81", {"center": v(0, 120) * mm, "radius": 6 * mm});
            skArc(sketch, "E82", {"start": v(15, 120) * mm, "mid": v(0, 135) * mm, "end": v(-15, 120) * mm});
            skLineSegment(sketch, "E83", {"start": v(15, 120) * mm, "end": v(15, 108) * mm});
            skLineSegment(sketch, "E84", {"start": v(-15, 120) * mm, "end": v(-15, 108) * mm});
            skLineSegment(sketch, "E85", {"start": v(-15, 108) * mm, "end": v(-33, 90) * mm});
            skLineSegment(sketch, "E86", {"start": v(15, 108) * mm, "end": v(33, 90) * mm});
            skLineSegment(sketch, "E87", {"start": v(-80, 0) * mm, "end": v(80, 0) * mm, "construction": true});
            skLineSegment(sketch, "E88.MirrorCS", {"start": v(-15, -108) * mm, "end": v(-33, -90) * mm});
            skLineSegment(sketch, "E89.MirrorCS", {"start": v(-15, -120) * mm, "end": v(-15, -108) * mm});
            skArc(sketch, "E90.MirrorCS", {"start": v(15, -120) * mm, "mid": v(0, -135) * mm, "end": v(-15, -120) * mm});
            skCircle(sketch, "E91.MirrorC", {"center": v(0, -120) * mm, "radius": 6 * mm});
            skLineSegment(sketch, "E92.MirrorCS", {"start": v(0, -120) * mm, "end": v(0, -90) * mm, "construction": true});
            skLineSegment(sketch, "E93.MirrorCS", {"start": v(15, -120) * mm, "end": v(15, -108) * mm});
            skLineSegment(sketch, "E94.MirrorCS", {"start": v(15, -108) * mm, "end": v(33, -90) * mm});
            skSolve(sketch);
        }
        {
            var Q0;
            Q0=makeQuery(id+"F16.imprint","IMPRINT",FACE,{"disambiguationData":[TD([[makeQuery(id+"F16.imprint","IMPRINT",EDGE,{"derivedFrom":sQuery(id+"F16.wireOp",EDGE,"E81")}),-1.0]])]});
            var Q1;
            {var subQ0=sQuery(id+"F16.wireOp",EDGE,"E88.MirrorCS");Q1=makeQuery(id+"F16.imprint","IMPRINT",FACE,{"disambiguationData":[TD([[makeQuery(id+"F16.imprint","IMPRINT",EDGE,{"derivedFrom":subQ0}),-1.0]])]});}
            var Q2;
            {var subQ5=sQuery(id+"F16.wireOp",EDGE,"E79.1");Q2=makeQuery(id+"F16.imprint","IMPRINT",FACE,{"disambiguationData":[TD([[makeQuery(id+"F16.imprint","IMPRINT",EDGE,{"derivedFrom":subQ5}),1.0]])]});}
            var Q3;
            Q3=makeQuery(id+"F2.opExtrude","CAP_FACE",FACE,{"disambiguationData":[OSD([sQuery(id+"F0.wireOp",EDGE,"E12"),sQuery(id+"F0.wireOp",EDGE,"E13"),sQuery(id+"F0.wireOp",EDGE,"E14"),sQuery(id+"F0.wireOp",EDGE,"E15"),sQuery(id+"F0.wireOp",EDGE,"E17.filletArc"),sQuery(id+"F0.wireOp",EDGE,"E18.filletArc"),sQuery(id+"F0.wireOp",EDGE,"E19.filletArc"),sQuery(id+"F0.wireOp",EDGE,"E20.filletArc"),sQuery(id+"F0.wireOp",EDGE,"E25.0"),sQuery(id+"F0.wireOp",EDGE,"E25.1"),sQuery(id+"F0.wireOp",EDGE,"E25.2"),sQuery(id+"F0.wireOp",EDGE,"E25.3"),sQuery(id+"F0.wireOp",EDGE,"E25.4"),sQuery(id+"F0.wireOp",EDGE,"E25.5"),sQuery(id+"F0.wireOp",EDGE,"E25.6"),sQuery(id+"F0.wireOp",EDGE,"E25.7")])],"isStart":false});
            extrude(context, id + "F17", {"entities" : qUnion([Q0, Q1, Q2]), "endBound" : BoundingType.UP_TO_SURFACE, "depth" : 25 * mm, "endBoundEntityFace" : qUnion([Q3]), "offsetDistance" : 25 * mm});
        }
    });
